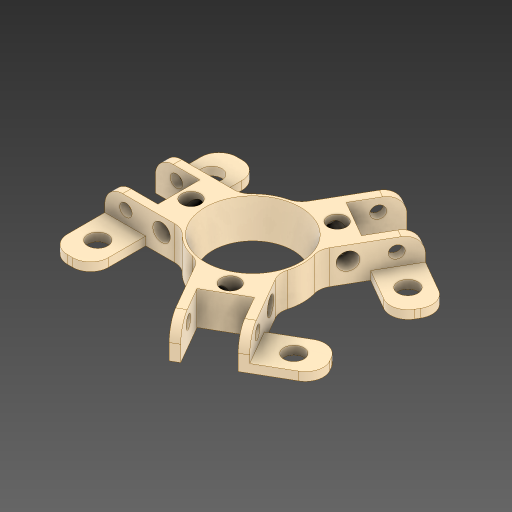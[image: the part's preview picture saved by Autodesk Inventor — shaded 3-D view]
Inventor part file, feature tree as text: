
AUTODESK INVENTOR PART (.ipt)
format: ipt  version: 2024 (Build 280153000, 153)  size: 631,296 bytes
history: native  units: in
note: dims shown in document units (in); Inventor stores cm internally (conversion verified against a paired STEP export)
features: sketch x4, hole x3, extrude x2, pattern_circular x2, other x1, fillet x1, draft x1, projected_geometry x1
ambient origin geometry x8: Origin, YZ Plane, XZ Plane, XY Plane, X Axis, Y Axis, Z Axis, Center Point
bodies: Solid1 (feature_tree)
feature tree (15):
  other  "Nut/Rod Template"
  extrude  "Spring Holder"  Depth=0.2618in
  hole  "Spring Pin Hole"  [1 undecoded]
  pattern_circular  "Pin Pattern"  [2 undecoded]
  extrude  "Plate"  Depth=1.4in
  hole  "MNTG Holes"  [1 undecoded]
  fillet  ".25" Filet"  Radius=1.6in
  hole  "Set Screw Holes"  [1 undecoded]
  draft  "FaceDraft1"
  pattern_circular  "Circular Pattern2"  [2 undecoded]
  sketch  "Sketch2"  dims[d6=0.8661in d10=0.2618in]
  sketch  "Sketch5"  dims[d11=0.5906in d13=0.1703in]
  sketch  "Sketch12"  dims[d14=0.1181in]
  sketch  "Sketch14"  dims[d17=1.125in d18=0.625in d19=1.4in d20=1.1811in d22=360.0deg d24=1.6in d25=2.75in d26=0.4724in d27=0.0in d31=0.1732in d32=0.75in d33=0.375in d34=0.25in d35=0.5635in d36=1.0in d37=0.8108in d39=0.2953in d40=0.1772in d55=1.1811in d56=360.0deg d60=0.4493in d61=0.7874in d63=1.6in d64=0.7874in d66=2.75in d77=0.281in d78=0.75in d79=0.875in d80=0.25in d81=0.5635in d82=1.0in d83=0.8108in d93=0.0618in d94=0.0618in d95=0.1272in d96=0.1272in d97=0.0564in d99=0.1181in d100=0.0in d104=0.0564in d107=0.118in d108=0.118in d109=0.25in d111=0.2441in d112=0.315in d113=0.375in d114=0.25in d115=0.5635in d116=0.315in d117=0.0in d118=0.1969in d119=0.0859in d120=1.1811in d121=360.0deg]
  projected_geometry  "Projected Loop2"
note: 7 required parameter values undecoded (feature->parameter linkage not recoverable at this tier; creation-order binding heuristic only, values carry confidence <= 0.55)
